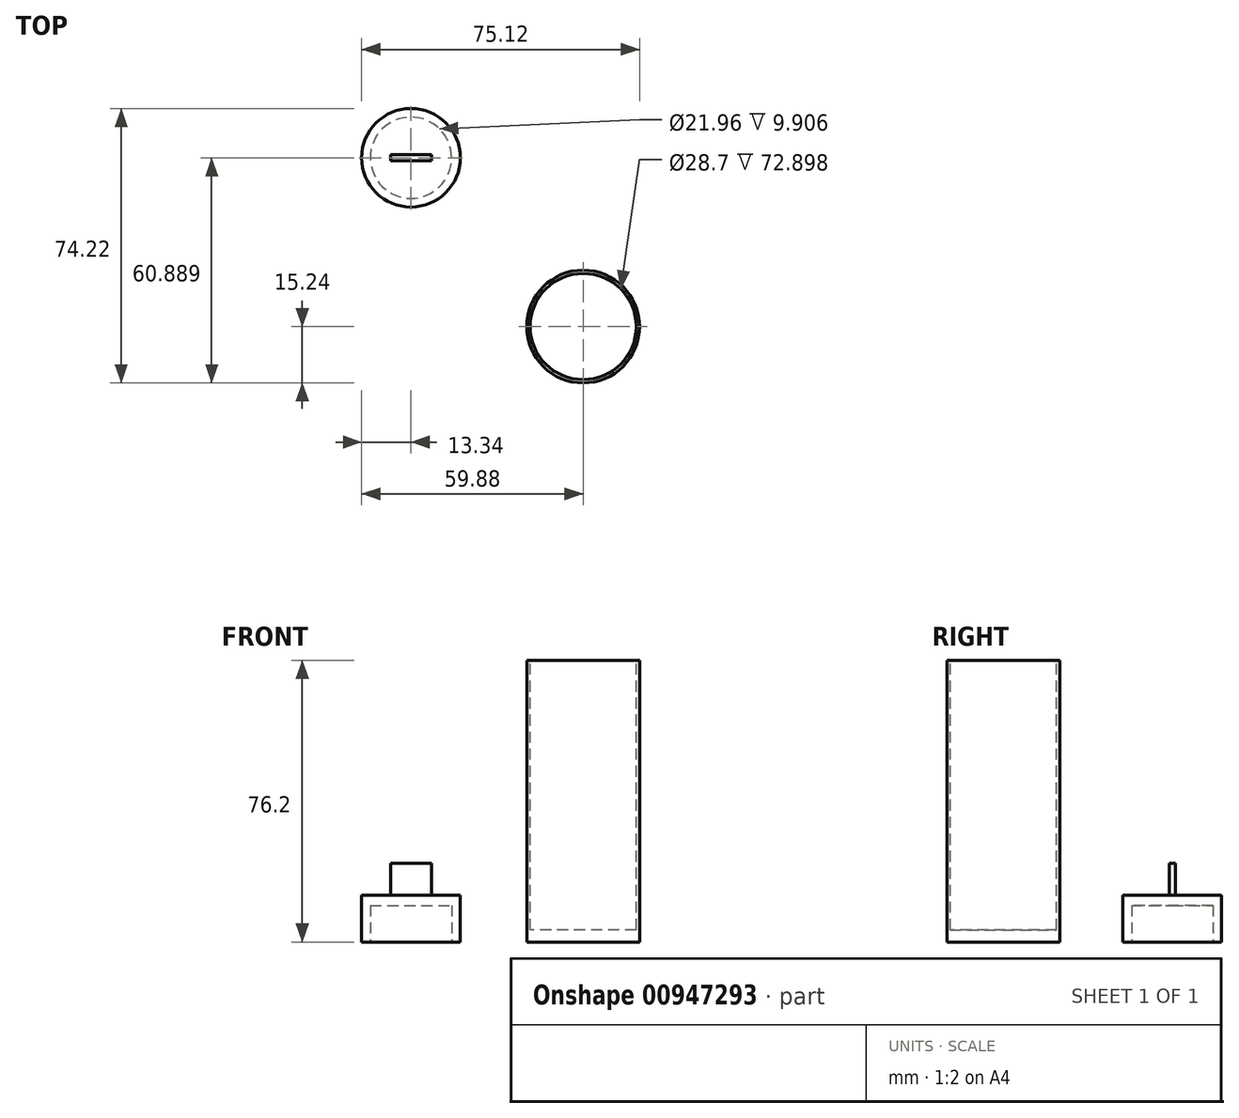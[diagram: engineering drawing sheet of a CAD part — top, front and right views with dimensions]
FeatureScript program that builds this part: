
annotation { "Feature Type Name" : "Feature", "Feature Type Description" : "" }
export const myFeature = defineFeature(function(context is Context, id is Id, definition is map)
    precondition{}
    {
        {
            var Q0;
            Q0=qCreatedBy(makeId("Top.planeOp"),FACE);
            var sketch = newSketch(context, id + "F0", { "sketchPlane" : qUnion([Q0])});
            skCircle(sketch, "E0", {"center": v(0, 0) * mm, "radius": 15.24 * mm});
            skSolve(sketch);
        }
        {
            var Q0;
            Q0 = qSketchRegion(id + "F0", true);
            extrude(context, id + "F1", {"entities" : qUnion([Q0]), "flatOperationType" : FlatOperationType.REMOVE, "depth" : 76.2 * mm, "offsetDistance" : 25.4 * mm, "domain" : OperationDomain.MODEL});
        }
        {
            var Q0;
            Q0=makeQuery(id+"F1.opExtrude","CAP_FACE",FACE,{"disambiguationData":[OSD([sQuery(id+"F0.wireOp",EDGE,"E0")])],"isStart":false});
            var sketch = newSketch(context, id + "F2", { "sketchPlane" : qUnion([Q0])});
            skCircle(sketch, "E1", {"center": v(0, 0) * mm, "radius": 14.35 * mm});
            skSolve(sketch);
        }
        {
            var Q0;
            Q0 = qSketchRegion(id + "F2", true);
            extrude(context, id + "F3", {"entities" : qUnion([Q0]), "operationType" : NewBodyOperationType.REMOVE, "flatOperationType" : FlatOperationType.REMOVE, "oppositeDirection" : true, "depth" : 72.9 * mm, "offsetDistance" : 25.4 * mm, "domain" : OperationDomain.MODEL});
        }
        {
            var Q0;
            Q0=qCreatedBy(makeId("Top.planeOp"),FACE);
            var sketch = newSketch(context, id + "F4", { "sketchPlane" : qUnion([Q0])});
            skCircle(sketch, "E2", {"center": v(-46.54, 45.65) * mm, "radius": 13.34 * mm});
            skSolve(sketch);
        }
        {
            var Q0;
            Q0 = qSketchRegion(id + "F4", true);
            extrude(context, id + "F5", {"entities" : qUnion([Q0]), "depth" : 12.7 * mm, "offsetDistance" : 25.4 * mm});
        }
        {
            var Q0;
            Q0=makeQuery(id+"F5.opExtrude","CAP_FACE",FACE,{"disambiguationData":[OSD([sQuery(id+"F4.wireOp",EDGE,"E2")])],"isStart":true});
            var sketch = newSketch(context, id + "F6", { "sketchPlane" : qUnion([Q0])});
            skCircle(sketch, "E3", {"center": v(-46.54, -45.65) * mm, "radius": 10.98 * mm});
            skSolve(sketch);
        }
        {
            var Q0;
            Q0 = qSketchRegion(id + "F6", true);
            extrude(context, id + "F7", {"entities" : qUnion([Q0]), "operationType" : NewBodyOperationType.REMOVE, "oppositeDirection" : true, "depth" : 9.9 * mm, "offsetDistance" : 25.4 * mm});
        }
        {
            var Q0;
            Q0=makeQuery(id+"F5.opExtrude","CAP_FACE",FACE,{"disambiguationData":[OSD([sQuery(id+"F4.wireOp",EDGE,"E2")])],"isStart":false});
            var sketch = newSketch(context, id + "F8", { "sketchPlane" : qUnion([Q0])});
            skLineSegment(sketch, "E4.bottom", {"start": v(-41, 44.86) * mm, "end": v(-52.09, 44.86) * mm});
            skLineSegment(sketch, "E4.top", {"start": v(-41, 46.44) * mm, "end": v(-52.09, 46.44) * mm});
            skLineSegment(sketch, "E4.left", {"start": v(-41, 44.86) * mm, "end": v(-41, 46.44) * mm});
            skLineSegment(sketch, "E4.right", {"start": v(-52.09, 44.86) * mm, "end": v(-52.09, 46.44) * mm});
            skPoint(sketch, "E4.middle", {"position": v(-46.54, 45.65) * mm});
            skSolve(sketch);
        }
        {
            var Q0;
            Q0 = qSketchRegion(id + "F8", true);
            extrude(context, id + "F9", {"entities" : qUnion([Q0]), "operationType" : NewBodyOperationType.ADD, "depth" : 8.64 * mm, "offsetDistance" : 25.4 * mm});
        }
    });
